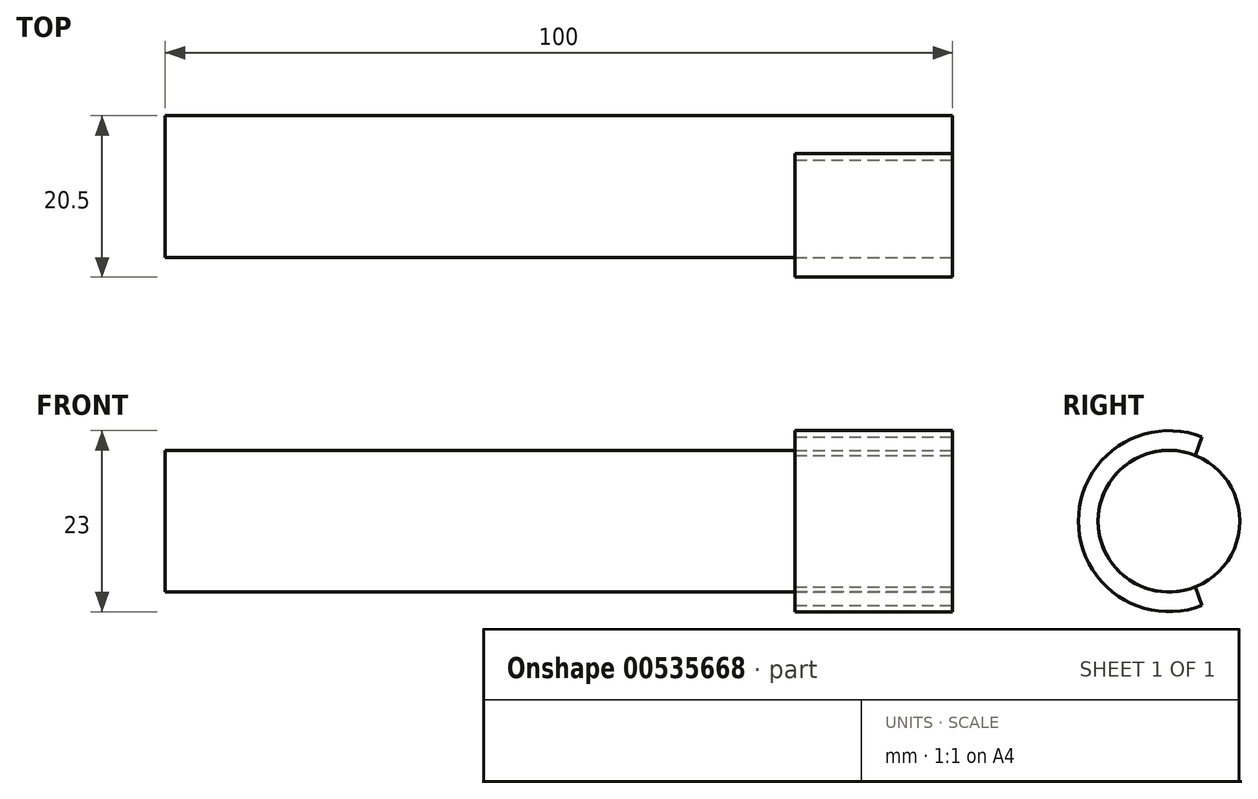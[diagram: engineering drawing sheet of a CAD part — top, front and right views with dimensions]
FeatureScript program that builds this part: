
annotation { "Feature Type Name" : "Feature", "Feature Type Description" : "" }
export const myFeature = defineFeature(function(context is Context, id is Id, definition is map)
    precondition{}
    {
        {
            var Q0;
            Q0=qCreatedBy(makeId("Right.planeOp"),FACE);
            var sketch = newSketch(context, id + "F0", { "sketchPlane" : qUnion([Q0])});
            skCircle(sketch, "E0", {"center": v(0, 0) * mm, "radius": 9 * mm});
            skSolve(sketch);
        }
        {
            var Q0;
            Q0 = qSketchRegion(id + "F0", true);
            extrude(context, id + "F1", {"entities" : qUnion([Q0]), "depth" : 100 * mm, "offsetDistance" : 25 * mm});
        }
        {
            var Q0;
            Q0=makeQuery(id+"F1.opExtrude","CAP_FACE",FACE,{"disambiguationData":[OSD([sQuery(id+"F0.wireOp",EDGE,"E0")])],"isStart":false});
            var sketch = newSketch(context, id + "F2", { "sketchPlane" : qUnion([Q0])});
            skArc(sketch, "E1.0", {"start": v(3.36, 8.35) * mm, "mid": v(-9, 0) * mm, "end": v(3.36, -8.35) * mm});
            skLineSegment(sketch, "E2", {"start": v(0, 9) * mm, "end": v(0, -9) * mm, "construction": true});
            skArc(sketch, "E3", {"start": v(4.21, 10.7) * mm, "mid": v(-11.5, 0) * mm, "end": v(4.21, -10.7) * mm});
            skLineSegment(sketch, "E4", {"start": v(3.36, 8.35) * mm, "end": v(4.21, 10.7) * mm});
            skLineSegment(sketch, "E5", {"start": v(3.36, 8.35) * mm, "end": v(3.36, -8.35) * mm, "construction": true});
            skLineSegment(sketch, "E6", {"start": v(3.36, -8.35) * mm, "end": v(4.21, -10.7) * mm});
            skSolve(sketch);
        }
        {
            var Q0;
            Q0 = qSketchRegion(id + "F2", true);
            extrude(context, id + "F3", {"entities" : qUnion([Q0]), "oppositeDirection" : true, "depth" : 20 * mm, "offsetDistance" : 25 * mm});
        }
    });
